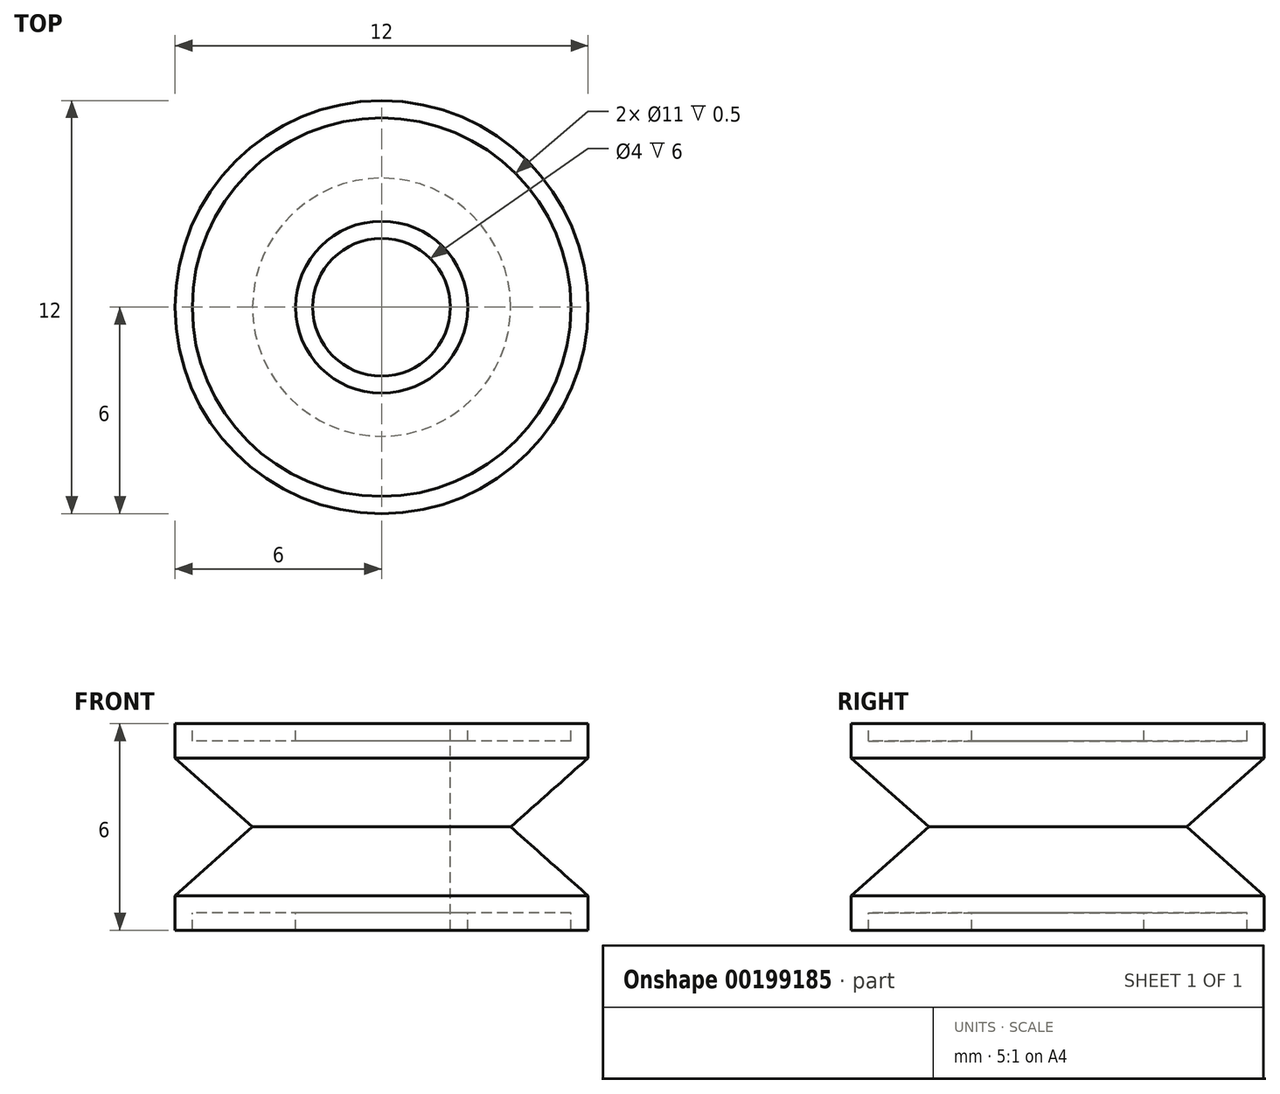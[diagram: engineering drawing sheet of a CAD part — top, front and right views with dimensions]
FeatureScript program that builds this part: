
annotation { "Feature Type Name" : "Feature", "Feature Type Description" : "" }
export const myFeature = defineFeature(function(context is Context, id is Id, definition is map)
    precondition{}
    {
        {
            var Q0;
            Q0=qCreatedBy(makeId("Front.planeOp"),FACE);
            var sketch = newSketch(context, id + "F0", { "sketchPlane" : qUnion([Q0])});
            skPoint(sketch, "E0", {"position": v(-6, 5) * mm});
            skLineSegment(sketch, "E1", {"start": v(-6, 5) * mm, "end": v(-3.75, 3) * mm});
            skLineSegment(sketch, "E2.trimOffspring", {"start": v(-6, 5) * mm, "end": v(-6, 6) * mm});
            skLineSegment(sketch, "E3.top", {"start": v(-2.5, 5.5) * mm, "end": v(-5.5, 5.5) * mm});
            skLineSegment(sketch, "E3.left", {"start": v(-2.5, 6) * mm, "end": v(-2.5, 5.5) * mm});
            skLineSegment(sketch, "E3.right", {"start": v(-5.5, 6) * mm, "end": v(-5.5, 5.5) * mm});
            skLineSegment(sketch, "E4", {"start": v(-6, 6) * mm, "end": v(-5.5, 6) * mm});
            skLineSegment(sketch, "E5", {"start": v(-2.5, 6) * mm, "end": v(-2, 6) * mm});
            skLineSegment(sketch, "E6", {"start": v(-2, 6) * mm, "end": v(-2, 3) * mm});
            skLineSegment(sketch, "E7", {"start": v(0, 3) * mm, "end": v(0, 6) * mm});
            skLineSegment(sketch, "E8.MirrorCS", {"start": v(-2.5, 0) * mm, "end": v(-2, 0) * mm});
            skPoint(sketch, "E9.MirrorP", {"position": v(-6, 1) * mm});
            skLineSegment(sketch, "E10.MirrorCS", {"start": v(-2.5, 0.5) * mm, "end": v(-5.5, 0.5) * mm});
            skLineSegment(sketch, "E11.MirrorCS", {"start": v(-6, 1) * mm, "end": v(-3.75, 3) * mm});
            skLineSegment(sketch, "E12.MirrorCS", {"start": v(0, 3) * mm, "end": v(0, 0) * mm});
            skLineSegment(sketch, "E13.MirrorCS", {"start": v(-5.5, 0) * mm, "end": v(-5.5, 0.5) * mm});
            skLineSegment(sketch, "E14.MirrorCS", {"start": v(-2.5, 0) * mm, "end": v(-2.5, 0.5) * mm});
            skLineSegment(sketch, "E15.MirrorCS", {"start": v(-2, 0) * mm, "end": v(-2, 3) * mm});
            skLineSegment(sketch, "E16.MirrorCS", {"start": v(-6, 1) * mm, "end": v(-6, 0) * mm});
            skLineSegment(sketch, "E17.MirrorCS", {"start": v(-6, 0) * mm, "end": v(-5.5, 0) * mm});
            skLineSegment(sketch, "E18", {"start": v(0, 6) * mm, "end": v(0, 0) * mm});
            skSolve(sketch);
        }
        {
            var Q0;
            Q0=makeQuery(id+"F0.imprint","IMPRINT",FACE,{"disambiguationData":[TD([[makeQuery(id+"F0.imprint","IMPRINT",EDGE,{"derivedFrom":sQuery(id+"F0.wireOp",EDGE,"E1")}),1.0]])]});
            var Q1;
            Q1=sQuery(id+"F0.wireOp",EDGE,"E18");
            revolve(context, id + "F1", {"entities" : qUnion([Q0]), "axis" : qUnion([Q1]), "revolveType" : RevolveType.FULL});
        }
    });
